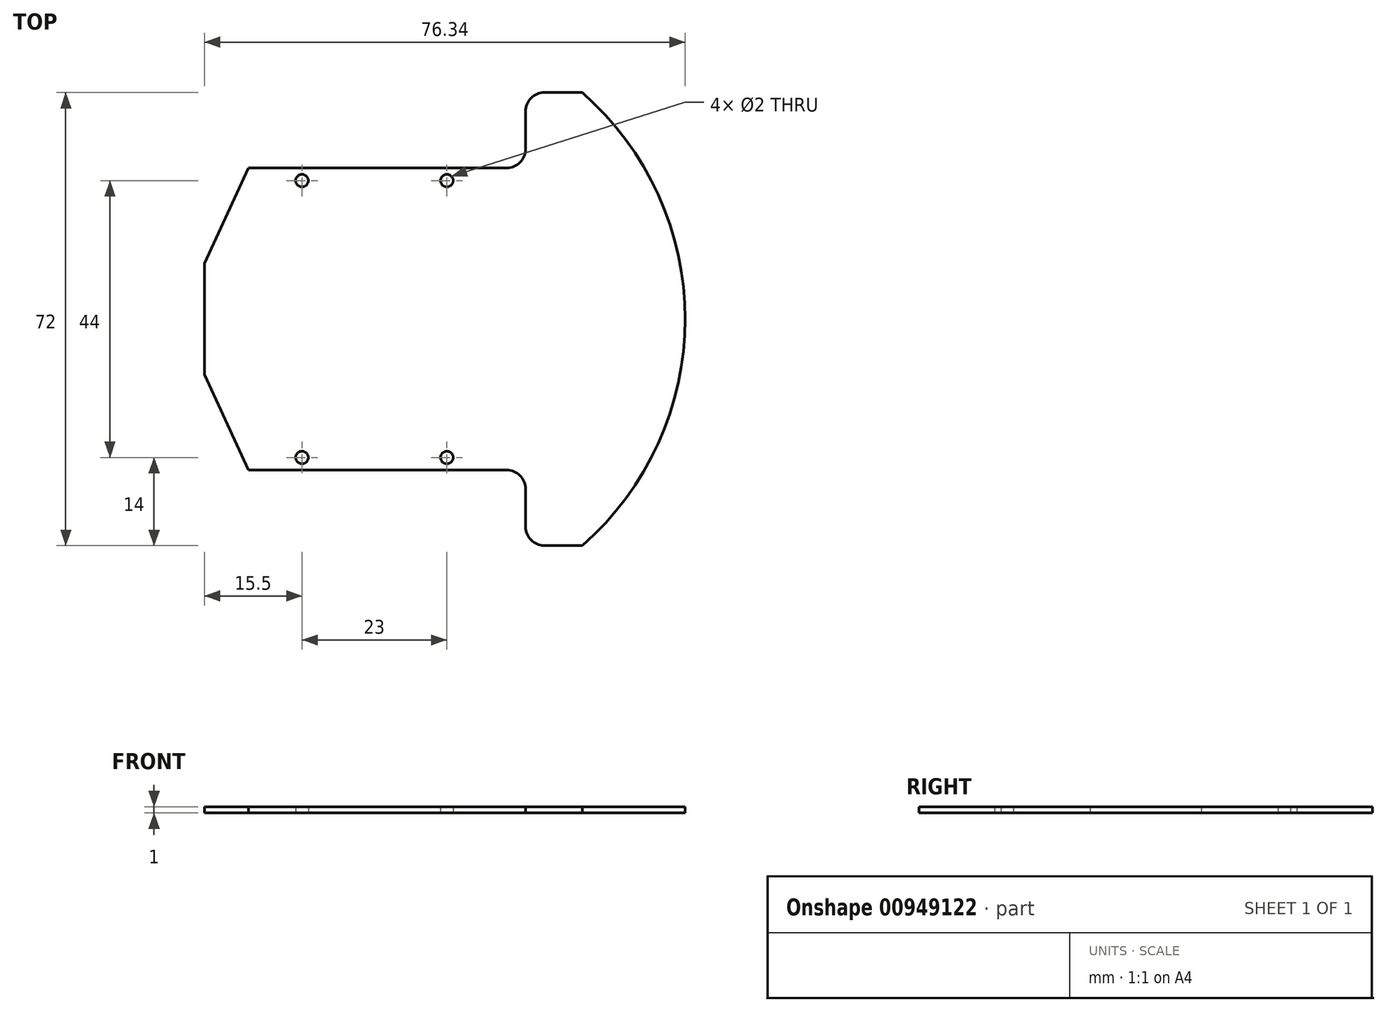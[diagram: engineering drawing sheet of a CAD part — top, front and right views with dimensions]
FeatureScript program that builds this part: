
annotation { "Feature Type Name" : "Feature", "Feature Type Description" : "" }
export const myFeature = defineFeature(function(context is Context, id is Id, definition is map)
    precondition{}
    {
        {
            var Q0;
            Q0=qCreatedBy(makeId("Top.planeOp"),FACE);
            var sketch = newSketch(context, id + "F0", { "sketchPlane" : qUnion([Q0])});
            skPoint(sketch, "E0", {"position": v(11.5, 22) * mm});
            skLineSegment(sketch, "E1", {"start": v(0, 24) * mm, "end": v(24, 24) * mm});
            skLineSegment(sketch, "E2.MirrorCS", {"start": v(0, -24) * mm, "end": v(24, -24) * mm});
            skLineSegment(sketch, "E3", {"start": v(24, 24) * mm, "end": v(24, 36) * mm});
            skLineSegment(sketch, "E4.MirrorCS", {"start": v(24, -24) * mm, "end": v(24, -36) * mm});
            skLineSegment(sketch, "E5", {"start": v(24, 36) * mm, "end": v(33, 36) * mm});
            skLineSegment(sketch, "E6.MirrorCS", {"start": v(24, -36) * mm, "end": v(33, -36) * mm});
            skPoint(sketch, "E7", {"position": v(49.34, 0) * mm});
            skArc(sketch, "E8", {"start": v(33, -36) * mm, "mid": v(49.34, 0) * mm, "end": v(33, 36) * mm});
            skLineSegment(sketch, "E9.1", {"start": v(0, 20) * mm, "end": v(24, 20) * mm, "construction": true});
            skLineSegment(sketch, "E10.0", {"start": v(8.5, 0) * mm, "end": v(8.5, 20) * mm, "construction": true});
            skLineSegment(sketch, "E11", {"start": v(0, -24) * mm, "end": v(-20, -24) * mm});
            skLineSegment(sketch, "E12", {"start": v(-20, -24) * mm, "end": v(-27, -8.83) * mm});
            skLineSegment(sketch, "E13", {"start": v(-27, -8.83) * mm, "end": v(-27, 0) * mm});
            skLineSegment(sketch, "E14.MirrorCS", {"start": v(-27, 8.83) * mm, "end": v(-27, 0) * mm});
            skLineSegment(sketch, "E15.MirrorCS", {"start": v(-20, 24) * mm, "end": v(-27, 8.83) * mm});
            skLineSegment(sketch, "E16.MirrorCS", {"start": v(0, 24) * mm, "end": v(-20, 24) * mm});
            skPoint(sketch, "E17.MirrorP", {"position": v(-11.5, 22) * mm});
            skPoint(sketch, "E18.MirrorP", {"position": v(-11.5, -22) * mm});
            skCircle(sketch, "E19", {"center": v(11.5, 22) * mm, "radius": 1 * mm});
            skLineSegment(sketch, "E20.MirrorCS", {"start": v(-8.5, 0) * mm, "end": v(-8.5, 20) * mm, "construction": true});
            skLineSegment(sketch, "E21.MirrorCS", {"start": v(0, 20) * mm, "end": v(-24, 20) * mm, "construction": true});
            skCircle(sketch, "E22.MirrorC", {"center": v(-11.5, 22) * mm, "radius": 1 * mm});
            skLineSegment(sketch, "E23.MirrorCS", {"start": v(8.5, 0) * mm, "end": v(8.5, -20) * mm, "construction": true});
            skLineSegment(sketch, "E24.MirrorCS", {"start": v(-8.5, 0) * mm, "end": v(-8.5, -20) * mm, "construction": true});
            skCircle(sketch, "E25.MirrorC", {"center": v(11.5, -22) * mm, "radius": 1 * mm});
            skCircle(sketch, "E26.MirrorC", {"center": v(-11.5, -22) * mm, "radius": 1 * mm});
            skSolve(sketch);
        }
        {
            var Q0;
            Q0=makeQuery(id+"F0.imprint","IMPRINT",FACE,{"disambiguationData":[TD([[makeQuery(id+"F0.imprint","IMPRINT",EDGE,{"derivedFrom":sQuery(id+"F0.wireOp",EDGE,"E1")}),-1.0]])]});
            extrude(context, id + "F1", {"entities" : qUnion([Q0]), "offsetDistance" : 25 * mm, "depth" : 1 * mm});
        }
        {
            var Q0;
            Q0=makeQuery(id+"F1.opExtrude","SWEPT_EDGE",EDGE,{"disambiguationData":[OSD([sQuery(id+"F0.wireOp",EDGE,"E3"),sQuery(id+"F0.wireOp",EDGE,"rtYzGScB-LIza-3EyH-c4Y1-TE7FodCweAnZ")])]});
            var Q1;
            Q1=makeQuery(id+"F1.opExtrude","SWEPT_EDGE",EDGE,{"disambiguationData":[OSD([sQuery(id+"F0.wireOp",EDGE,"rtYzGScB-LIza-3EyH-c4Y1-TE7FodCweAnZ"),sQuery(id+"F0.wireOp",EDGE,"vQnKk0Fm-p07t-lp9N-pp2g-1DoQWshYwX53")])]});
            var Q2;
            Q2=makeQuery(id+"F1.opExtrude","SWEPT_EDGE",EDGE,{"disambiguationData":[OSD([sQuery(id+"F0.wireOp",EDGE,"926122f4-e5da-4837-b1c0-6a08add72fdd0.MirrorCS"),sQuery(id+"F0.wireOp",EDGE,"ac9621fe-2715-497c-96b4-4551774b6d720.MirrorCS")])]});
            var Q3;
            Q3=makeQuery(id+"F1.opExtrude","SWEPT_EDGE",EDGE,{"disambiguationData":[OSD([sQuery(id+"F0.wireOp",EDGE,"ac9621fe-2715-497c-96b4-4551774b6d720.MirrorCS"),sQuery(id+"F0.wireOp",EDGE,"216b550c-1359-4a71-919e-f2a60b3f459c0.MirrorCS")])]});
            var Q4;
            Q4=makeQuery(id+"F1.opExtrude","SWEPT_EDGE",EDGE,{"disambiguationData":[OSD([sQuery(id+"F0.wireOp",EDGE,"59f9b107-8d20-4550-a8d7-751e5877622e0.MirrorCS"),sQuery(id+"F0.wireOp",EDGE,"644c1389-629c-4f66-8f66-4d6adeb715910.MirrorCS")])]});
            var Q5;
            Q5=makeQuery(id+"F1.opExtrude","SWEPT_EDGE",EDGE,{"disambiguationData":[OSD([sQuery(id+"F0.wireOp",EDGE,"644c1389-629c-4f66-8f66-4d6adeb715910.MirrorCS"),sQuery(id+"F0.wireOp",EDGE,"216b550c-1359-4a71-919e-f2a60b3f459c0.MirrorCS")])]});
            var Q6;
            Q6=makeQuery(id+"F1.opExtrude","SWEPT_EDGE",EDGE,{"disambiguationData":[OSD([sQuery(id+"F0.wireOp",EDGE,"vQnKk0Fm-p07t-lp9N-pp2g-1DoQWshYwX53"),sQuery(id+"F0.wireOp",EDGE,"2eb57afa-1c2e-4598-a542-6dcb4fcd98f00.MirrorCS")])]});
            var Q7;
            Q7=makeQuery(id+"F1.opExtrude","SWEPT_EDGE",EDGE,{"disambiguationData":[OSD([sQuery(id+"F0.wireOp",EDGE,"E4.MirrorCS"),sQuery(id+"F0.wireOp",EDGE,"2eb57afa-1c2e-4598-a542-6dcb4fcd98f00.MirrorCS")])]});
            fillet(context, id + "F2", {"entities" : qUnion([Q0, Q1, Q2, Q3, Q4, Q5, Q6, Q7]), "radius" : 3 * mm, "tangentPropagation" : true, "allowEdgeOverflow" : false});
        }
    });
